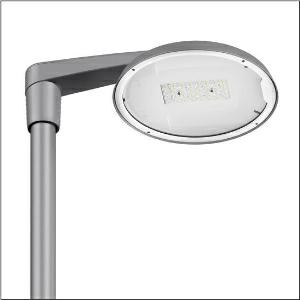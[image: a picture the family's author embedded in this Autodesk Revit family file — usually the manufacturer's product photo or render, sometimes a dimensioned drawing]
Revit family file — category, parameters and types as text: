
# Revit family: dl_r__50_iq_mini___st0_5a_5xa248b41f08je_3ec1
name_source: partatom
category: Lighting Fixtures
units: mm (PartAtom-declared; Revit-internal decimal feet)

## family parameters
Cut with Voids When Loaded = No
Host = Face
Light Source = No
Part Type = Normal
Room Calculation Point = No
Round Connector Dimension = Use Diameter
Shared = No

## types (1)
- --- (1 x LED, 10300 lm, 62.6 W, 4000K)
    Apparent Load = 63 VA
    CIE Flux Codes = 43 76 97 100 100
    Color Rendering = 70
    Color Temperature = 4000K
    Default Elevation = 1800 mm
    Description = DL® 50 iQ mini, mast luminaire, primary light control with lens, of PMMA, primary optical cover: cover, of toughened safety glass, transparent, light distribution: ST0.5a, light emission: direct distribution, primary light characteristic: asymmetric, installation type: side-entry, post-top, LED, High Power LED, rated luminous flux: 10.300lm, luminous efficacy: 165lm/W, light colour: 740, colour temperature: 4000K, control: optimised constant luminous flux control (CLO 2.0), Desk-Remote (wireless, voltage-free reading and setting of iQ features in the workshop via application-optimized NFC function/RFID function), Light-Fading, Smart-Wire, Night-Set, Lumen-Switch, Temp-Guard, Auto-Match, Street-Remote, mains connection: 230..240V, AC, 50/60Hz, connection cable pre-assembled, cable length: 8,5m, start of lifetime: 63W, end of service life: 65W, reduction: 29W, luminaire housing, of diecast aluminium, powder-coated, Siteco® metallic grey (DB 702S), inclination adjustable: 0°, 5°, 10° (post-top) | 0°, -5°, -10°, -15° (side-entry), please order mast post-top element or mast side-entry element separately, diameter: 500mm, height: 115mm, post-top: for spigot size d x l = 76 x 100mm; with reducer (optional accessory) 60 x 100mm | side-entry: for spigot size d x l = 60 x 100mm; with reducer (optional accessory) 42 x 100mm, protection rating (complete): IP66, insulation class (complete): insulation class II (safety insulation), certification: CE, ENEC, VDE, impact resistance: IK08, permissible operating ambient temperature for outdoor applications: -25..+40°C, standard-compliant lighting for roads and squares, packaging unit: 1 piece

Light Distribution: ST0.5a
    Height = 115 mm
    Lamp = 1 x LED
    Lamp Light Flux = 10300 lm
    Lamp Power = 62.6 W
    Lamp count = 1
    Length = 500 mm
    Luminous efficacy = 165 lm/W
    Manufacturer = Siteco
    ModVariant = No
    Model = 5XA248B41F08JE
    Number of Poles = 1
    OnlyDefault = Yes
    Power Factor = 1
    Product Name = DL® 50 iQ mini | ST0.5a
    Product group = mast luminaire | pylon top
    ProductGroupID = 6100
    Protection Class = Protection class II
    Protection Degree = IP 66
    RLX_Detail_Level = 1
    RLX_Emergency_Light_Flux = 0 lm
    RLX_Emergency_Type = 0
    RLX_Emergency_Type_DB = No
    RlxData = <blob elided: 126785 chars, md5=796da808>
    Socket = socket
    Standby Power = 0 W
    System Light Flux = 10300 lm
    System Power = 63 W
    Type Comments = factory setting: luminous flux: 100 % | dim-lin: 254 | 658 mA
    Type Image = l_1251794.jpg
    URL = http://relux.com
    VarID = @adj_092251
    Voltage = 0 V
    Weight = 0.00 kg
    Width = 0 mm  [stored 0 ft]

note: [stored X ft] marks values corroborated as IEEE doubles in the binary element streams (Revit-internal decimal feet)

## geometry (parser evidence)
native form markers: Blend x4, Sweep x10
no freeform markers — native parametric forms only
